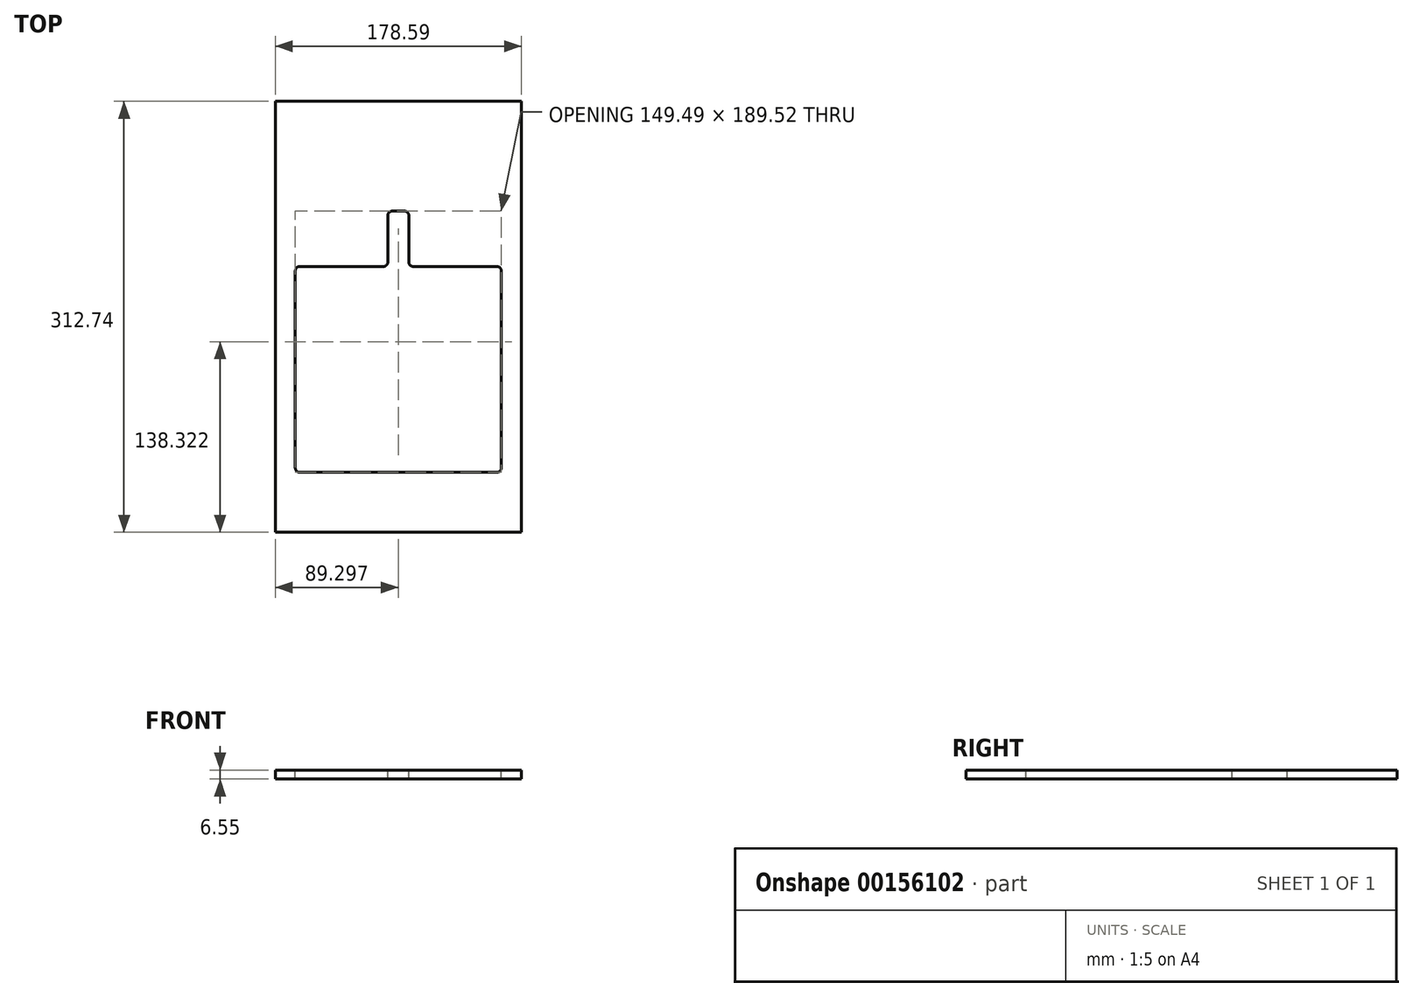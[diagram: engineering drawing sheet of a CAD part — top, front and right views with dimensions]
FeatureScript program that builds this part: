
annotation { "Feature Type Name" : "Feature", "Feature Type Description" : "" }
export const myFeature = defineFeature(function(context is Context, id is Id, definition is map)
    precondition{}
    {
        {
            var Q0;
            Q0=qCreatedBy(makeId("Top.planeOp"),FACE);
            var sketch = newSketch(context, id + "F0", { "sketchPlane" : qUnion([Q0])});
            skLineSegment(sketch, "E0.bottom", {"start": v(0, 0) * mm, "end": v(178.6, 0) * mm});
            skLineSegment(sketch, "E0.top", {"start": v(0, 312.74) * mm, "end": v(178.6, 312.74) * mm});
            skLineSegment(sketch, "E0.left", {"start": v(0, 0) * mm, "end": v(0, 312.74) * mm});
            skLineSegment(sketch, "E0.right", {"start": v(178.6, 0) * mm, "end": v(178.6, 312.74) * mm});
            skSolve(sketch);
        }
        {
            var Q0;
            Q0=qSketchRegion(id+"F0",true);
            extrude(context, id + "F1", {"entities" : qUnion([Q0]), "depth" : 6.55 * mm});
        }
        {
            var Q0;
            Q0=makeQuery(id+"F1.opExtrude","CAP_FACE",FACE,{"disambiguationData":[OSD([sQuery(id+"F0.wireOp",EDGE,"E0.bottom"),sQuery(id+"F0.wireOp",EDGE,"E0.top"),sQuery(id+"F0.wireOp",EDGE,"E0.left"),sQuery(id+"F0.wireOp",EDGE,"E0.right")])],"isStart":false});
            var sketch = newSketch(context, id + "F2", { "sketchPlane" : qUnion([Q0])});
            skLineSegment(sketch, "E1.bottom", {"start": v(17.73, 192.95) * mm, "end": v(78.5, 192.95) * mm});
            skLineSegment(sketch, "E1.top", {"start": v(17.73, 43.56) * mm, "end": v(160.86, 43.56) * mm});
            skLineSegment(sketch, "E1.left", {"start": v(14.55, 189.78) * mm, "end": v(14.55, 46.74) * mm});
            skLineSegment(sketch, "E1.right", {"start": v(164.04, 189.78) * mm, "end": v(164.04, 46.74) * mm});
            skLineSegment(sketch, "E2", {"start": v(89.3, 312.74) * mm, "end": v(89.3, 0) * mm, "construction": true});
            skLineSegment(sketch, "E3", {"start": v(81.68, 196.13) * mm, "end": v(81.68, 229.9) * mm});
            skLineSegment(sketch, "E4", {"start": v(96.92, 196.13) * mm, "end": v(96.92, 229.9) * mm});
            skLineSegment(sketch, "E5", {"start": v(84.85, 233.08) * mm, "end": v(93.74, 233.08) * mm});
            skLineSegment(sketch, "E6.trimOffspring", {"start": v(100.1, 192.95) * mm, "end": v(160.86, 192.95) * mm});
            skPoint(sketch, "E7.visualSharp", {"position": v(14.55, 192.95) * mm});
            skArc(sketch, "E7.filletArc", {"start": v(17.73, 192.95) * mm, "mid": v(15.48, 192.02) * mm, "end": v(14.55, 189.78) * mm});
            skPoint(sketch, "E8.visualSharp", {"position": v(14.55, 43.56) * mm});
            skArc(sketch, "E8.filletArc", {"start": v(14.55, 46.74) * mm, "mid": v(15.48, 44.5) * mm, "end": v(17.73, 43.56) * mm});
            skPoint(sketch, "E9.visualSharp", {"position": v(164.04, 43.56) * mm});
            skArc(sketch, "E9.filletArc", {"start": v(160.86, 43.56) * mm, "mid": v(163.1, 44.5) * mm, "end": v(164.04, 46.74) * mm});
            skPoint(sketch, "E10.visualSharp", {"position": v(164.04, 192.95) * mm});
            skArc(sketch, "E10.filletArc", {"start": v(164.04, 189.78) * mm, "mid": v(163.1, 192.02) * mm, "end": v(160.86, 192.95) * mm});
            skPoint(sketch, "E11.visualSharp", {"position": v(96.92, 192.95) * mm});
            skArc(sketch, "E11.filletArc", {"start": v(96.92, 196.13) * mm, "mid": v(97.85, 193.88) * mm, "end": v(100.1, 192.95) * mm});
            skPoint(sketch, "E12.visualSharp", {"position": v(96.92, 233.08) * mm});
            skArc(sketch, "E12.filletArc", {"start": v(96.92, 229.9) * mm, "mid": v(95.99, 232.15) * mm, "end": v(93.74, 233.08) * mm});
            skPoint(sketch, "E13.visualSharp", {"position": v(81.68, 233.08) * mm});
            skArc(sketch, "E13.filletArc", {"start": v(84.85, 233.08) * mm, "mid": v(82.6, 232.15) * mm, "end": v(81.68, 229.9) * mm});
            skPoint(sketch, "E14.visualSharp", {"position": v(81.68, 192.95) * mm});
            skArc(sketch, "E14.filletArc", {"start": v(78.5, 192.95) * mm, "mid": v(80.75, 193.88) * mm, "end": v(81.68, 196.13) * mm});
            skSolve(sketch);
        }
        {
            var Q0;
            Q0=makeQuery(id+"F2.imprint","IMPRINT",FACE,{"disambiguationData":[TD([[makeQuery(id+"F2.imprint","IMPRINT",EDGE,{"derivedFrom":sQuery(id+"F2.wireOp",EDGE,"E1.bottom")}),-1.0]])]});
            extrude(context, id + "F3", {"entities" : qUnion([Q0]), "operationType" : NewBodyOperationType.REMOVE, "oppositeDirection" : true, "depth" : 25.4 * mm});
        }
    });
